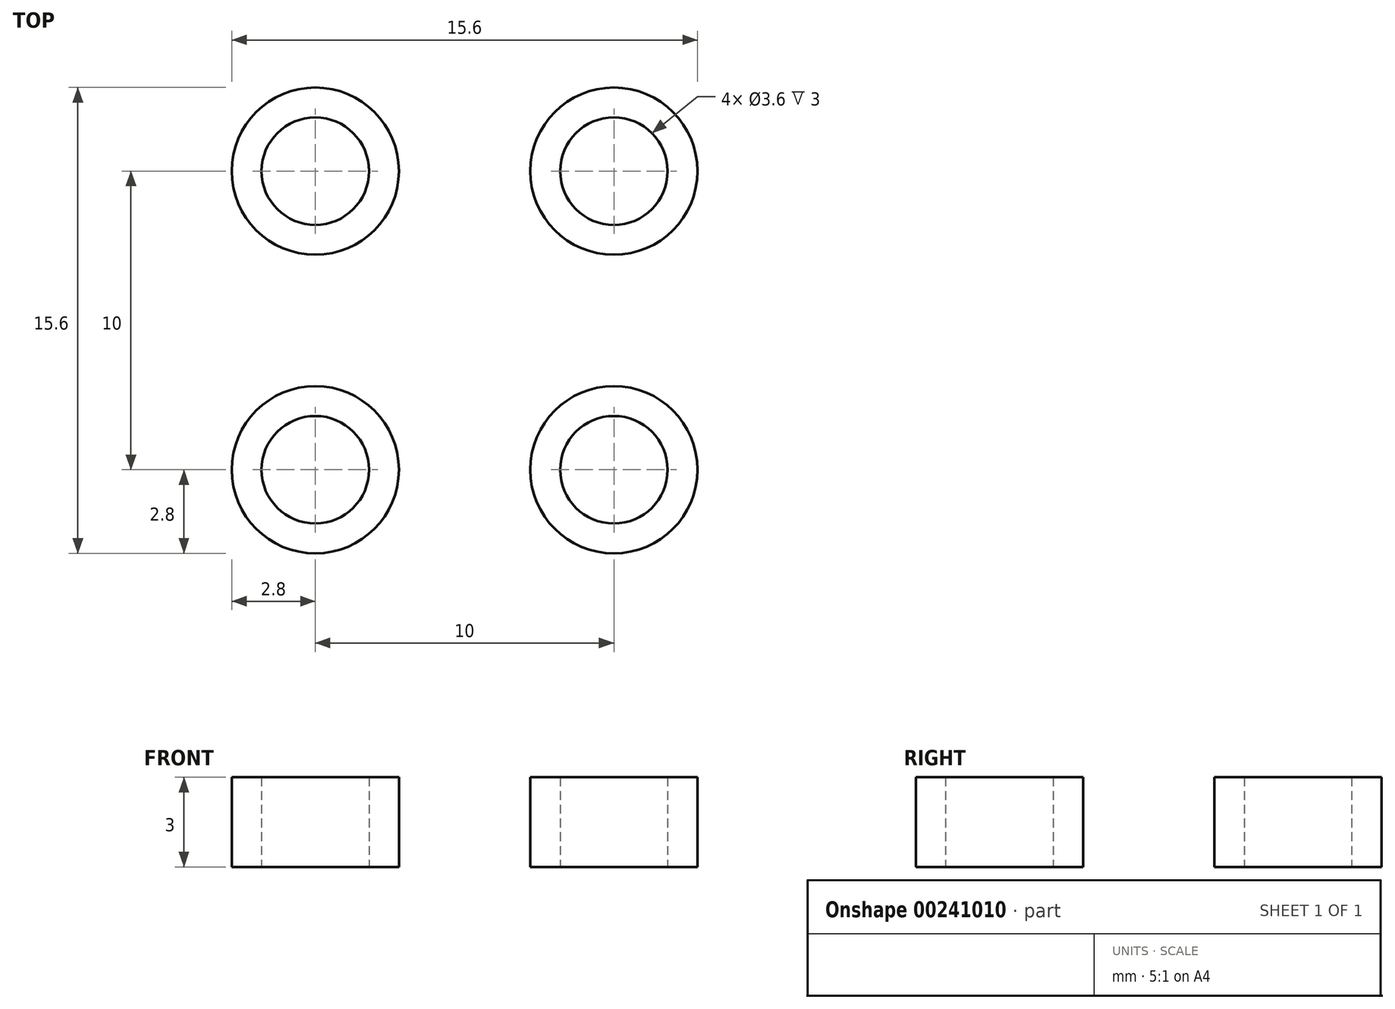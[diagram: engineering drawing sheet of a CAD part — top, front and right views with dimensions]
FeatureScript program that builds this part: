
annotation { "Feature Type Name" : "Feature", "Feature Type Description" : "" }
export const myFeature = defineFeature(function(context is Context, id is Id, definition is map)
    precondition{}
    {
        {
            var Q0;
            Q0=qCreatedBy(makeId("Top.planeOp"),FACE);
            var sketch = newSketch(context, id + "F0", { "sketchPlane" : qUnion([Q0])});
            skCircle(sketch, "E0", {"center": v(0, 0) * mm, "radius": 1.8 * mm});
            skCircle(sketch, "E1", {"center": v(0, 0) * mm, "radius": 2.8 * mm});
            skSolve(sketch);
        }
        {
            var Q0;
            Q0 = qSketchRegion(id + "F0", true);
            extrude(context, id + "F1", {"entities" : qUnion([Q0]), "depth" : 3 * mm});
        }
        {
            var Q0;
            Q0=makeQuery(id+"F1.opExtrude","SWEPT_BODY",BODY,{"disambiguationData":[OSD([sQuery(id+"F0.wireOp",EDGE,"E0"),sQuery(id+"F0.wireOp",EDGE,"E1")])]});
            transform(context, id + "F2", {"entities" : qUnion([Q0]), "transformType" : TransformType.TRANSLATION_3D, "dx" : 10 * mm, "dy" : 0 * mm, "dz" : 0 * mm, "makeCopy" : true});
        }
        {
            var Q0;
            Q0=makeQuery(id+"F1.opExtrude","SWEPT_BODY",BODY,{"disambiguationData":[OSD([sQuery(id+"F0.wireOp",EDGE,"E0"),sQuery(id+"F0.wireOp",EDGE,"E1")])]});
            var Q1;
            Q1=makeQuery(id+"F2.opPattern","COPY",BODY,{"derivedFrom":makeQuery(id+"F1.opExtrude","SWEPT_BODY",BODY,{"disambiguationData":[OSD([sQuery(id+"F0.wireOp",EDGE,"E0"),sQuery(id+"F0.wireOp",EDGE,"E1")])]}),"instanceName":"1"});
            transform(context, id + "F3", {"entities" : qUnion([Q0, Q1]), "transformType" : TransformType.TRANSLATION_3D, "dx" : 0 * mm, "dy" : 10 * mm, "dz" : 0 * mm, "makeCopy" : true});
        }
    });
